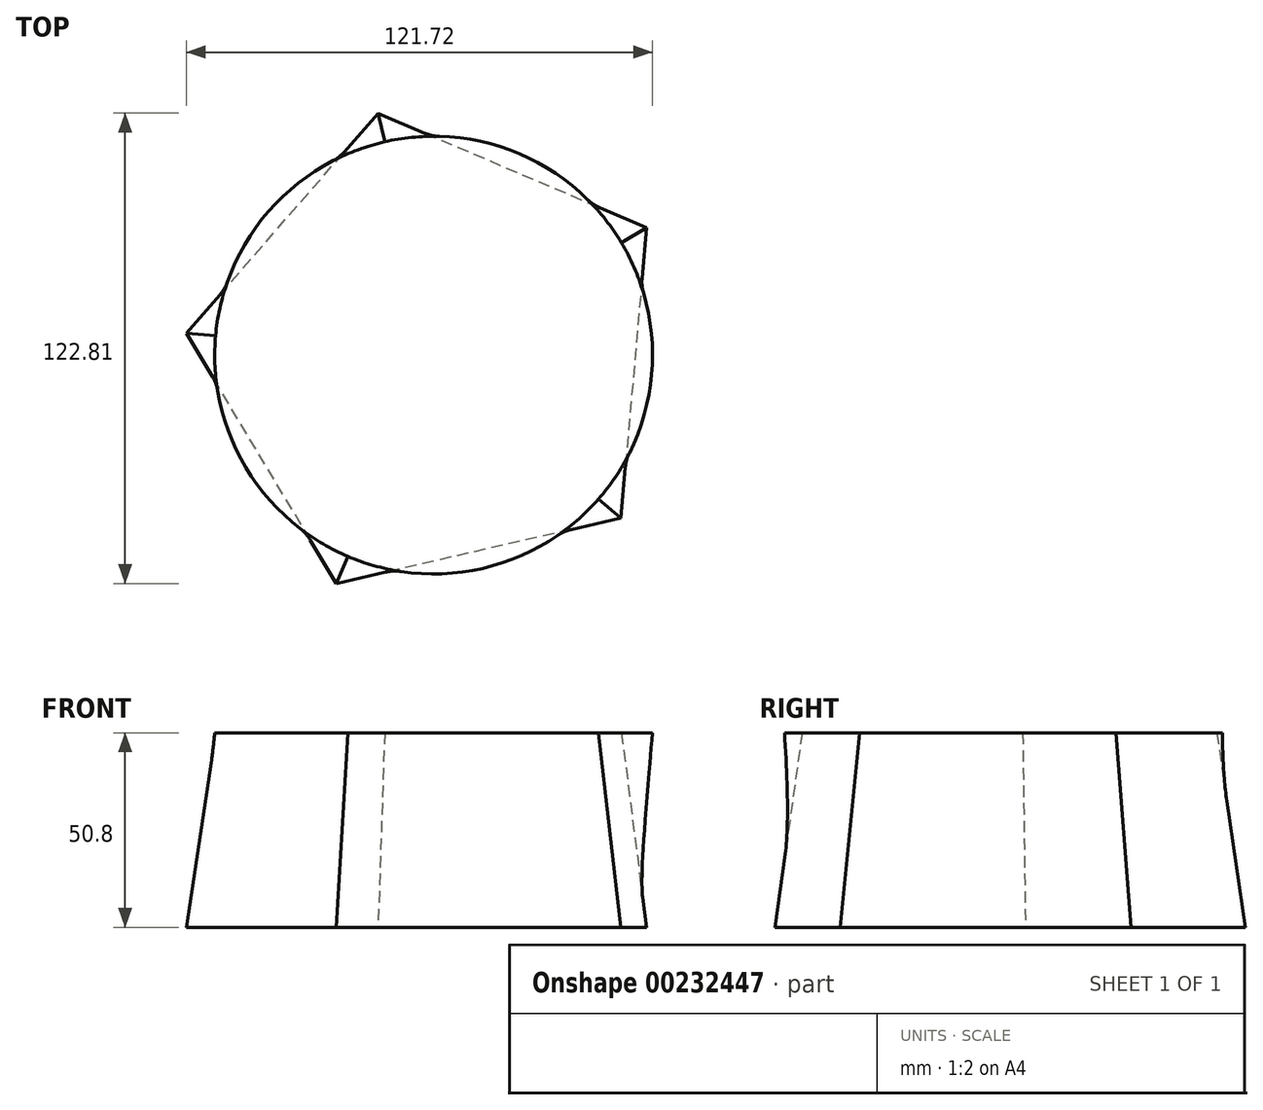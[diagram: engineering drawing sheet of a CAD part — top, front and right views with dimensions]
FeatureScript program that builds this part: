
annotation { "Feature Type Name" : "Feature", "Feature Type Description" : "" }
export const myFeature = defineFeature(function(context is Context, id is Id, definition is map)
    precondition{}
    {
        {
            var Q0;
            Q0=qCreatedBy(makeId("Top.planeOp"),FACE);
            var sketch = newSketch(context, id + "F0", { "sketchPlane" : qUnion([Q0])});
            skLineSegment(sketch, "E0.0", {"start": v(-25.4, -59.63) * mm, "end": v(-64.57, 5.73) * mm});
            skLineSegment(sketch, "E0.1", {"start": v(-64.57, 5.73) * mm, "end": v(-14.5, 63.18) * mm});
            skLineSegment(sketch, "E0.2", {"start": v(-14.5, 63.18) * mm, "end": v(55.6, 33.31) * mm});
            skLineSegment(sketch, "E0.3", {"start": v(55.6, 33.31) * mm, "end": v(48.87, -42.59) * mm});
            skLineSegment(sketch, "E0.4", {"start": v(48.87, -42.59) * mm, "end": v(-25.4, -59.63) * mm});
            skPoint(sketch, "E0.0.midPoint", {"position": v(-44.98, -26.95) * mm});
            skSolve(sketch);
        }
        {
            var Q0;
            Q0=makeQuery(id+"F0.imprint","IMPRINT",FACE,{"disambiguationData":[TD([[makeQuery(id+"F0.imprint","IMPRINT",EDGE,{"derivedFrom":sQuery(id+"F0.wireOp",EDGE,"E0.0")}),-1.0]])]});
            cPlane(context, id + "F1", {"entities" : qUnion([Q0]), "cplaneType" : CPlaneType.OFFSET, "offset" : 50.8 * mm, "width" : 152.4 * mm, "height" : 152.4 * mm});
        }
        {
            var Q0;
            Q0=qCreatedBy(id+"F1.planeOp",FACE);
            var sketch = newSketch(context, id + "F2", { "sketchPlane" : qUnion([Q0])});
            skCircle(sketch, "E1", {"center": v(0, 0) * mm, "radius": 57.15 * mm});
            skSolve(sketch);
        }
        {
            var Q0;
            Q0=makeQuery(id+"F2.imprint","IMPRINT",FACE,{"disambiguationData":[TD([[makeQuery(id+"F2.imprint","IMPRINT",EDGE,{"derivedFrom":sQuery(id+"F2.wireOp",EDGE,"E1")}),1.0]])]});
            var Q1;
            Q1=makeQuery(id+"F0.imprint","IMPRINT",FACE,{"disambiguationData":[TD([[makeQuery(id+"F0.imprint","IMPRINT",EDGE,{"derivedFrom":sQuery(id+"F0.wireOp",EDGE,"E0.0")}),-1.0]])]});
            loft(context, id + "F3", {"sheetProfilesArray" : [{ "sheetProfileEntities" : qUnion([Q0]) }, { "sheetProfileEntities" : qUnion([Q1]) }]});
        }
    });
